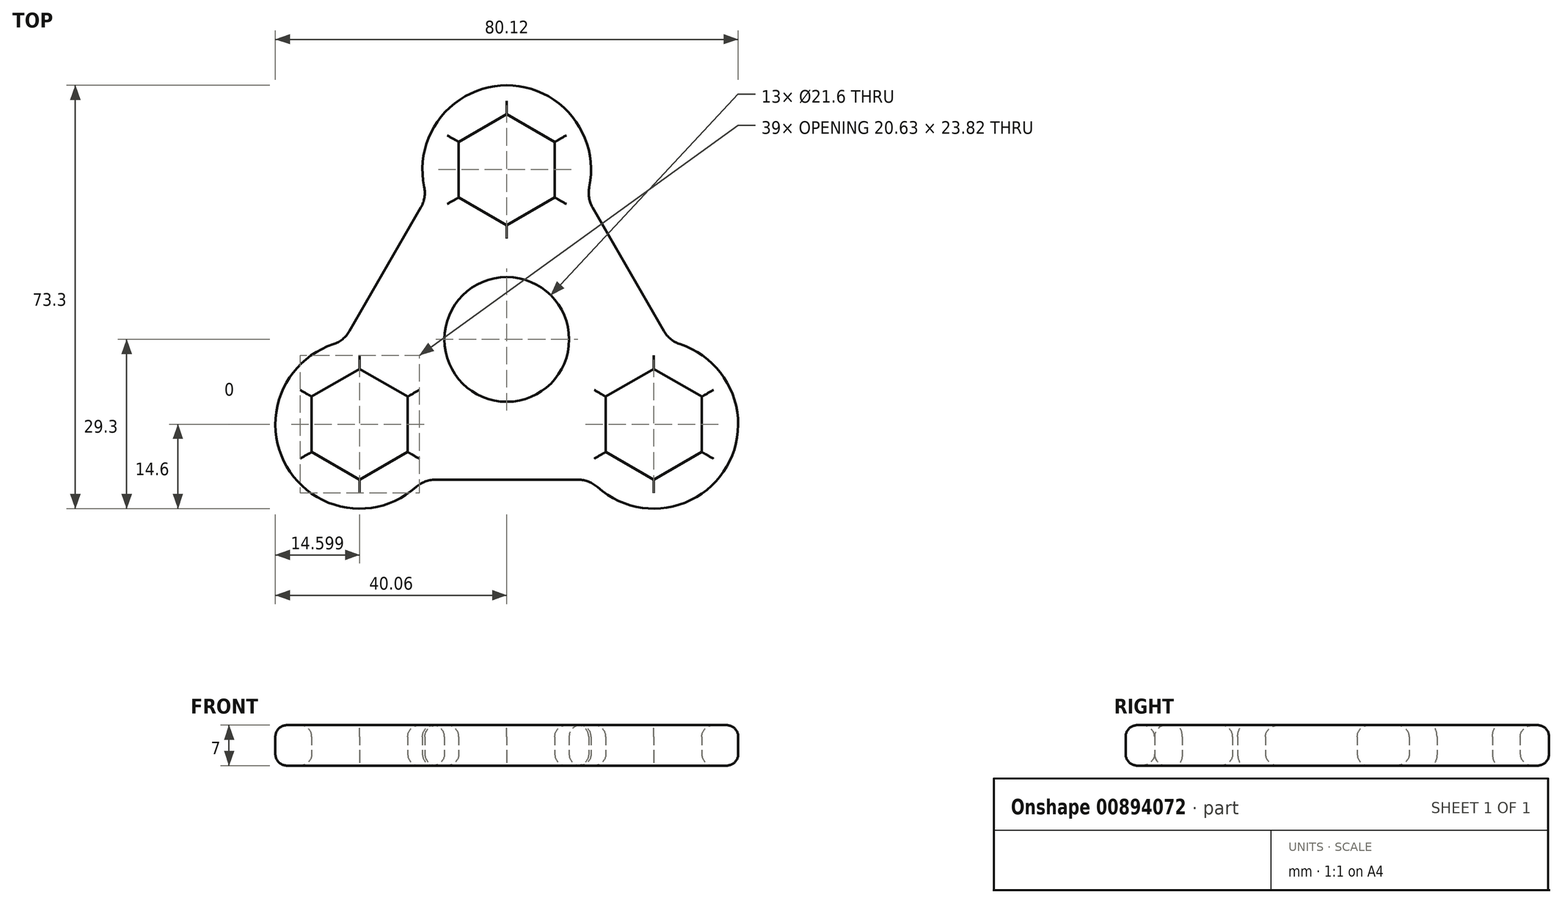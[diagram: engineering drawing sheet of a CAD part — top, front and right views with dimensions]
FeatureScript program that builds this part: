
annotation { "Feature Type Name" : "Feature", "Feature Type Description" : "" }
export const myFeature = defineFeature(function(context is Context, id is Id, definition is map)
    precondition{}
    {
        {
            var Q0;
            Q0=qCreatedBy(makeId("Top.planeOp"),FACE);
            var sketch = newSketch(context, id + "F0", { "sketchPlane" : qUnion([Q0])});
            skCircle(sketch, "E0", {"center": v(0, 0) * mm, "radius": 10.8 * mm});
            skLineSegment(sketch, "E1", {"start": v(0, 0) * mm, "end": v(0, 44) * mm, "construction": true});
            skLineSegment(sketch, "E2", {"start": v(0, 0) * mm, "end": v(38.1, -22) * mm, "construction": true});
            skLineSegment(sketch, "E3", {"start": v(0, 0) * mm, "end": v(-38.1, -22) * mm, "construction": true});
            skCircle(sketch, "E4.cCircle", {"center": v(0, 29.4) * mm, "radius": 8.31 * mm, "construction": true});
            skLineSegment(sketch, "E4.0", {"start": v(8.31, 34.2) * mm, "end": v(8.31, 24.6) * mm});
            skLineSegment(sketch, "E4.1", {"start": v(8.31, 24.6) * mm, "end": v(0, 19.8) * mm});
            skLineSegment(sketch, "E4.2", {"start": v(0, 19.8) * mm, "end": v(-8.31, 24.6) * mm});
            skLineSegment(sketch, "E4.3", {"start": v(-8.31, 24.6) * mm, "end": v(-8.31, 34.2) * mm});
            skLineSegment(sketch, "E4.4", {"start": v(-8.31, 34.2) * mm, "end": v(0, 39) * mm});
            skLineSegment(sketch, "E4.5", {"start": v(0, 39) * mm, "end": v(8.31, 34.2) * mm});
            skPoint(sketch, "E4.0.midPoint", {"position": v(8.31, 29.4) * mm});
            skArc(sketch, "E5", {"start": v(14.29, 26.4) * mm, "mid": v(0, 44) * mm, "end": v(-14.29, 26.4) * mm});
            skCircle(sketch, "E6.cCircle", {"center": v(25.46, -14.7) * mm, "radius": 8.31 * mm, "construction": true});
            skLineSegment(sketch, "E6.0", {"start": v(25.46, -5.1) * mm, "end": v(33.77, -9.9) * mm});
            skLineSegment(sketch, "E6.1", {"start": v(33.77, -9.9) * mm, "end": v(33.77, -19.5) * mm});
            skLineSegment(sketch, "E6.2", {"start": v(33.77, -19.5) * mm, "end": v(25.46, -24.3) * mm});
            skLineSegment(sketch, "E6.3", {"start": v(25.46, -24.3) * mm, "end": v(17.15, -19.5) * mm});
            skLineSegment(sketch, "E6.4", {"start": v(17.15, -19.5) * mm, "end": v(17.15, -9.9) * mm});
            skLineSegment(sketch, "E6.5", {"start": v(17.15, -9.9) * mm, "end": v(25.46, -5.1) * mm});
            skPoint(sketch, "E6.0.midPoint", {"position": v(29.62, -7.5) * mm});
            skArc(sketch, "E7", {"start": v(15.72, -25.58) * mm, "mid": v(38.1, -22) * mm, "end": v(30, -0.83) * mm});
            skCircle(sketch, "E8.cCircle", {"center": v(-25.46, -14.7) * mm, "radius": 8.31 * mm, "construction": true});
            skLineSegment(sketch, "E8.0", {"start": v(-17.15, -19.5) * mm, "end": v(-25.46, -24.3) * mm});
            skLineSegment(sketch, "E8.1", {"start": v(-25.46, -24.3) * mm, "end": v(-33.77, -19.5) * mm});
            skLineSegment(sketch, "E8.2", {"start": v(-33.77, -19.5) * mm, "end": v(-33.77, -9.9) * mm});
            skLineSegment(sketch, "E8.3", {"start": v(-33.77, -9.9) * mm, "end": v(-25.46, -5.1) * mm});
            skLineSegment(sketch, "E8.4", {"start": v(-25.46, -5.1) * mm, "end": v(-17.15, -9.9) * mm});
            skLineSegment(sketch, "E8.5", {"start": v(-17.15, -9.9) * mm, "end": v(-17.15, -19.5) * mm});
            skPoint(sketch, "E8.0.midPoint", {"position": v(-21.3, -21.9) * mm});
            skArc(sketch, "E9", {"start": v(-30, -0.83) * mm, "mid": v(-38.1, -22) * mm, "end": v(-15.72, -25.58) * mm});
            skLineSegment(sketch, "E10", {"start": v(-27.24, 1.42) * mm, "end": v(-14.85, 22.88) * mm});
            skLineSegment(sketch, "E11", {"start": v(-12.38, -24.3) * mm, "end": v(12.38, -24.3) * mm});
            skLineSegment(sketch, "E12", {"start": v(27.24, 1.42) * mm, "end": v(14.85, 22.88) * mm});
            skPoint(sketch, "E13.visualSharp", {"position": v(-13.81, 24.67) * mm});
            skArc(sketch, "E13.filletArc", {"start": v(-14.85, 22.88) * mm, "mid": v(-14.24, 24.59) * mm, "end": v(-14.29, 26.4) * mm});
            skPoint(sketch, "E14.visualSharp", {"position": v(13.81, 24.67) * mm});
            skArc(sketch, "E14.filletArc", {"start": v(14.29, 26.4) * mm, "mid": v(14.24, 24.59) * mm, "end": v(14.85, 22.88) * mm});
            skPoint(sketch, "E15.visualSharp", {"position": v(28.27, -0.37) * mm});
            skArc(sketch, "E15.filletArc", {"start": v(27.24, 1.42) * mm, "mid": v(28.42, 0.04) * mm, "end": v(30, -0.83) * mm});
            skPoint(sketch, "E16.visualSharp", {"position": v(14.46, -24.3) * mm});
            skArc(sketch, "E16.filletArc", {"start": v(15.72, -25.58) * mm, "mid": v(14.17, -24.63) * mm, "end": v(12.38, -24.3) * mm});
            skPoint(sketch, "E17.visualSharp", {"position": v(-14.46, -24.3) * mm});
            skArc(sketch, "E17.filletArc", {"start": v(-12.38, -24.3) * mm, "mid": v(-14.17, -24.63) * mm, "end": v(-15.72, -25.58) * mm});
            skPoint(sketch, "E18.visualSharp", {"position": v(-28.27, -0.37) * mm});
            skArc(sketch, "E18.filletArc", {"start": v(-30, -0.83) * mm, "mid": v(-28.42, 0.04) * mm, "end": v(-27.24, 1.42) * mm});
            skSolve(sketch);
        }
        {
            var Q0;
            Q0=makeQuery(id+"F0.imprint","IMPRINT",FACE,{"disambiguationData":[TD([[makeQuery(id+"F0.imprint","IMPRINT",EDGE,{"derivedFrom":sQuery(id+"F0.wireOp",EDGE,"E0")}),-1.0]])]});
            extrude(context, id + "F1", {"entities" : qUnion([Q0]), "depth" : 7 * mm, "offsetDistance" : 25 * mm});
        }
        {
            var Q0;
            Q0=makeQuery(id+"F1.opExtrude","CAP_FACE",FACE,{"disambiguationData":[OSD([sQuery(id+"F0.wireOp",EDGE,"E0"),sQuery(id+"F0.wireOp",EDGE,"E4.0"),sQuery(id+"F0.wireOp",EDGE,"E4.1"),sQuery(id+"F0.wireOp",EDGE,"E4.2"),sQuery(id+"F0.wireOp",EDGE,"E4.3"),sQuery(id+"F0.wireOp",EDGE,"E4.4"),sQuery(id+"F0.wireOp",EDGE,"E4.5"),sQuery(id+"F0.wireOp",EDGE,"E5"),sQuery(id+"F0.wireOp",EDGE,"E6.0"),sQuery(id+"F0.wireOp",EDGE,"E6.1"),sQuery(id+"F0.wireOp",EDGE,"E6.2"),sQuery(id+"F0.wireOp",EDGE,"E6.3"),sQuery(id+"F0.wireOp",EDGE,"E6.4"),sQuery(id+"F0.wireOp",EDGE,"E6.5"),sQuery(id+"F0.wireOp",EDGE,"E7"),sQuery(id+"F0.wireOp",EDGE,"E8.0"),sQuery(id+"F0.wireOp",EDGE,"E8.1"),sQuery(id+"F0.wireOp",EDGE,"E8.2"),sQuery(id+"F0.wireOp",EDGE,"E8.3"),sQuery(id+"F0.wireOp",EDGE,"E8.4"),sQuery(id+"F0.wireOp",EDGE,"E8.5"),sQuery(id+"F0.wireOp",EDGE,"E9"),sQuery(id+"F0.wireOp",EDGE,"E10"),sQuery(id+"F0.wireOp",EDGE,"E11"),sQuery(id+"F0.wireOp",EDGE,"E12"),sQuery(id+"F0.wireOp",EDGE,"E13.filletArc"),sQuery(id+"F0.wireOp",EDGE,"E14.filletArc"),sQuery(id+"F0.wireOp",EDGE,"E15.filletArc"),sQuery(id+"F0.wireOp",EDGE,"E16.filletArc"),sQuery(id+"F0.wireOp",EDGE,"E17.filletArc"),sQuery(id+"F0.wireOp",EDGE,"E18.filletArc")])],"isStart":false});
            fillet(context, id + "F2", {"entities" : qUnion([Q0]), "radius" : 2 * mm, "tangentPropagation" : true, "allowEdgeOverflow" : false});
        }
        {
            var Q0;
            Q0=makeQuery(id+"F1.opExtrude","CAP_FACE",FACE,{"disambiguationData":[OSD([sQuery(id+"F0.wireOp",EDGE,"E0"),sQuery(id+"F0.wireOp",EDGE,"E4.0"),sQuery(id+"F0.wireOp",EDGE,"E4.1"),sQuery(id+"F0.wireOp",EDGE,"E4.2"),sQuery(id+"F0.wireOp",EDGE,"E4.3"),sQuery(id+"F0.wireOp",EDGE,"E4.4"),sQuery(id+"F0.wireOp",EDGE,"E4.5"),sQuery(id+"F0.wireOp",EDGE,"E5"),sQuery(id+"F0.wireOp",EDGE,"E6.0"),sQuery(id+"F0.wireOp",EDGE,"E6.1"),sQuery(id+"F0.wireOp",EDGE,"E6.2"),sQuery(id+"F0.wireOp",EDGE,"E6.3"),sQuery(id+"F0.wireOp",EDGE,"E6.4"),sQuery(id+"F0.wireOp",EDGE,"E6.5"),sQuery(id+"F0.wireOp",EDGE,"E7"),sQuery(id+"F0.wireOp",EDGE,"E8.0"),sQuery(id+"F0.wireOp",EDGE,"E8.1"),sQuery(id+"F0.wireOp",EDGE,"E8.2"),sQuery(id+"F0.wireOp",EDGE,"E8.3"),sQuery(id+"F0.wireOp",EDGE,"E8.4"),sQuery(id+"F0.wireOp",EDGE,"E8.5"),sQuery(id+"F0.wireOp",EDGE,"E9"),sQuery(id+"F0.wireOp",EDGE,"E10"),sQuery(id+"F0.wireOp",EDGE,"E11"),sQuery(id+"F0.wireOp",EDGE,"E12"),sQuery(id+"F0.wireOp",EDGE,"E13.filletArc"),sQuery(id+"F0.wireOp",EDGE,"E14.filletArc"),sQuery(id+"F0.wireOp",EDGE,"E15.filletArc"),sQuery(id+"F0.wireOp",EDGE,"E16.filletArc"),sQuery(id+"F0.wireOp",EDGE,"E17.filletArc"),sQuery(id+"F0.wireOp",EDGE,"E18.filletArc")])],"isStart":true});
            fillet(context, id + "F3", {"entities" : qUnion([Q0]), "radius" : 2 * mm, "tangentPropagation" : true, "allowEdgeOverflow" : false});
        }
    });
